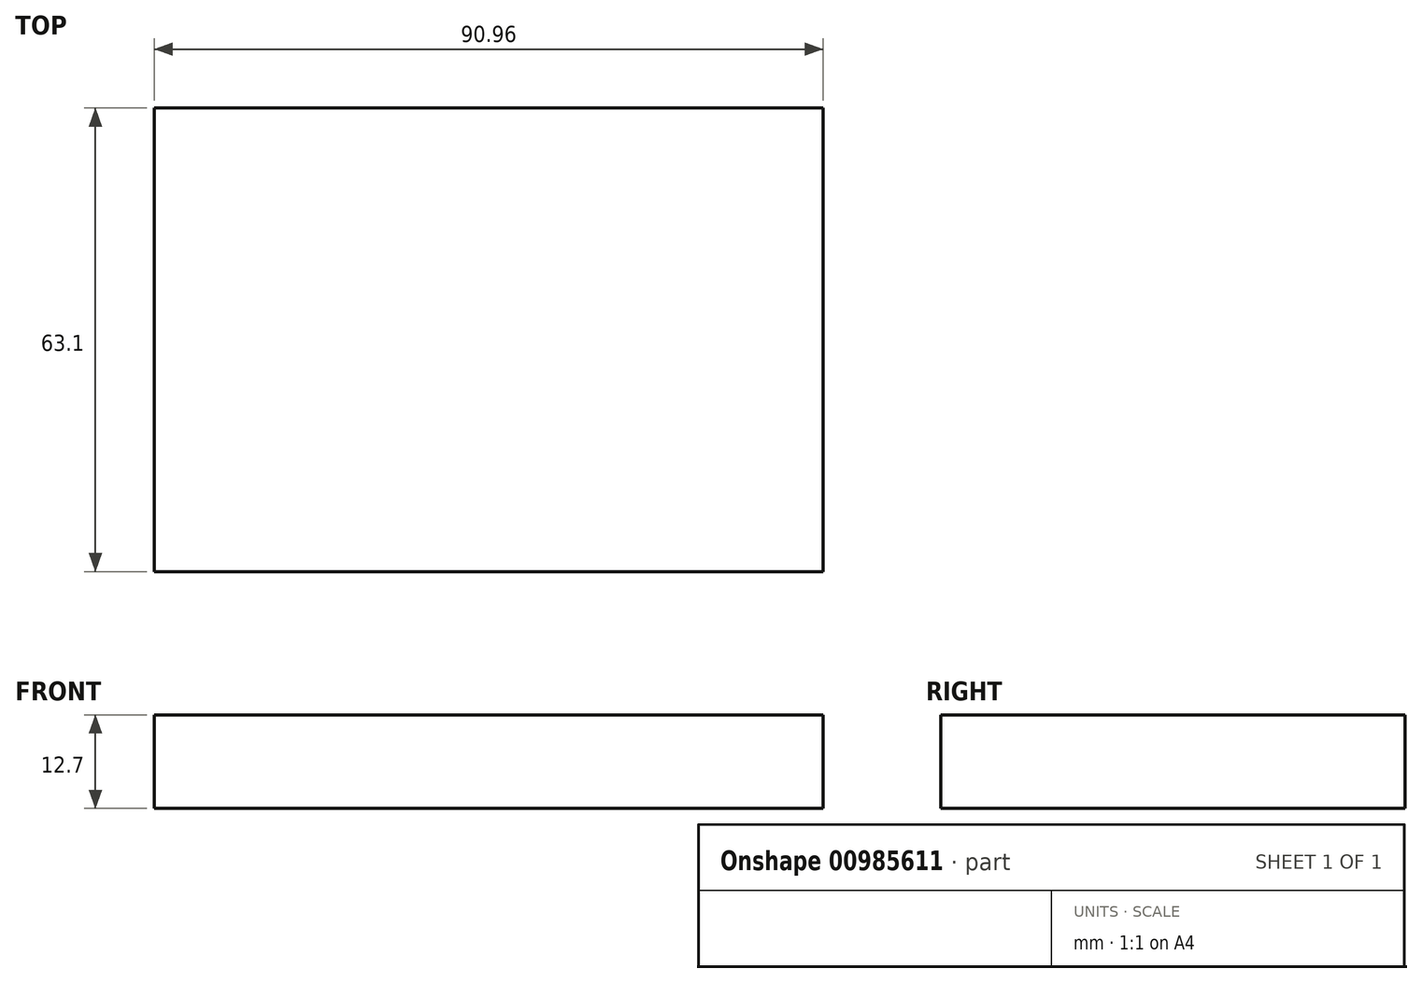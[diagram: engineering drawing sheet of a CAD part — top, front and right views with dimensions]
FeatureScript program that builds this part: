
annotation { "Feature Type Name" : "Feature", "Feature Type Description" : "" }
export const myFeature = defineFeature(function(context is Context, id is Id, definition is map)
    precondition{}
    {
        {
            var Q0;
            Q0=qCreatedBy(makeId("Top.planeOp"),FACE);
            var sketch = newSketch(context, id + "F0", { "sketchPlane" : qUnion([Q0])});
            skLineSegment(sketch, "E0.bottom", {"start": v(-45.48, 31.55) * mm, "end": v(45.48, 31.55) * mm});
            skLineSegment(sketch, "E0.top", {"start": v(-45.48, -31.55) * mm, "end": v(45.48, -31.55) * mm});
            skLineSegment(sketch, "E0.left", {"start": v(-45.48, 31.55) * mm, "end": v(-45.48, -31.55) * mm});
            skLineSegment(sketch, "E0.right", {"start": v(45.48, 31.55) * mm, "end": v(45.48, -31.55) * mm});
            skSolve(sketch);
        }
        {
            var Q0;
            Q0=makeQuery(id+"F0.imprint","IMPRINT",FACE,{"disambiguationData":[TD([[makeQuery(id+"F0.imprint","IMPRINT",EDGE,{"derivedFrom":sQuery(id+"F0.wireOp",EDGE,"E0.bottom")}),-1.0]])]});
            var Q1;
            Q1 = qSketchRegion(id + "F0", true);
            extrude(context, id + "F1", {"entities" : qUnion([Q0, Q1]), "depth" : 12.7 * mm, "offsetDistance" : 25.4 * mm});
        }
    });
